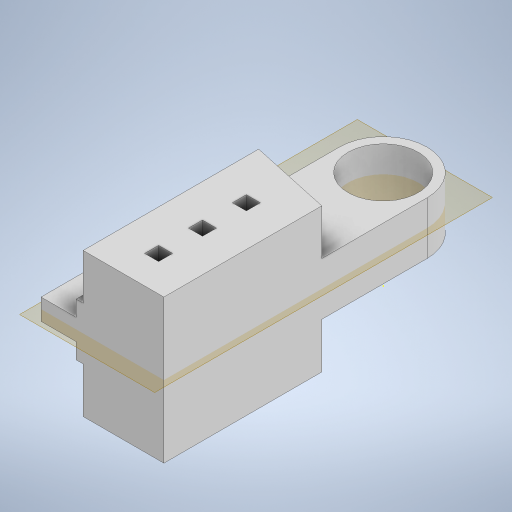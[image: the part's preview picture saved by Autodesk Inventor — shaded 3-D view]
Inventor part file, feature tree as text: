
AUTODESK INVENTOR PART (.ipt)
format: ipt  version: 2023 (Build 270158000, 158)  size: 336,384 bytes
history: native  units: mm
features: sketch x9, extrude x6, mirror x2, plane x1
ambient origin geometry x8: Origin, YZ Plane, XZ Plane, XY Plane, X Axis, Y Axis, Z Axis, Center Point
bodies: Solid1 (feature_tree)
feature tree (18):
  extrude  "Extrusion1"  Depth=25.0mm
  extrude  "Extrusion2"  Depth=15.0mm TaperAngle=0.0deg
  sketch  "Sketch3"  dims[d5=50.0mm d8=3.0mm]
  extrude  "Extrusion3"  Depth=3.0mm
  sketch  "Sketch5"  dims[d11=10.0mm d12=0.0mm d13=25.0mm d14=0.0mm]
  extrude  "Extrusion6"  Depth=50.0mm
  extrude  "Extrusion7"  Depth=25.0mm TaperAngle=0.0deg
  sketch  "Sketch10"  dims[d43=4.0mm]
  extrude  "Extrusion8"  Depth=4.0mm
  plane  "Work Plane1"
  mirror  "Mirror1"
  mirror  "Mirror2"
  sketch  "Sketch1"  dims[d0=20.0mm d1=25.0mm]
  sketch  "Sketch2"  dims[d2=50.0mm d3=15.0mm d4=0.0mm]
  sketch  "Sketch4"  dims[d9=6.0mm d10=50.0mm]
  sketch  "Sketch8"  dims[d40=4.0mm d41=4.0mm]
  sketch  "Sketch9"  dims[d42=13.0mm]
  sketch  "Sketch11"  dims[d44=4.0mm d45=13.0mm d46=4.0mm d47=4.0mm d48=10.0mm d49=0.0mm d50=30.0mm d51=2.0mm d52=13.0mm d53=0.0mm d54=11.5mm d55=4.0mm d56=4.0mm d57=12.5mm d58=4.0mm d59=4.0mm d60=12.5mm d61=4.0mm d62=4.0mm d63=50.0mm d64=0.0mm d65=7.5mm d36=0.5mm d37=0.872665mm d38=0.5mm d39=0.872665mm]
